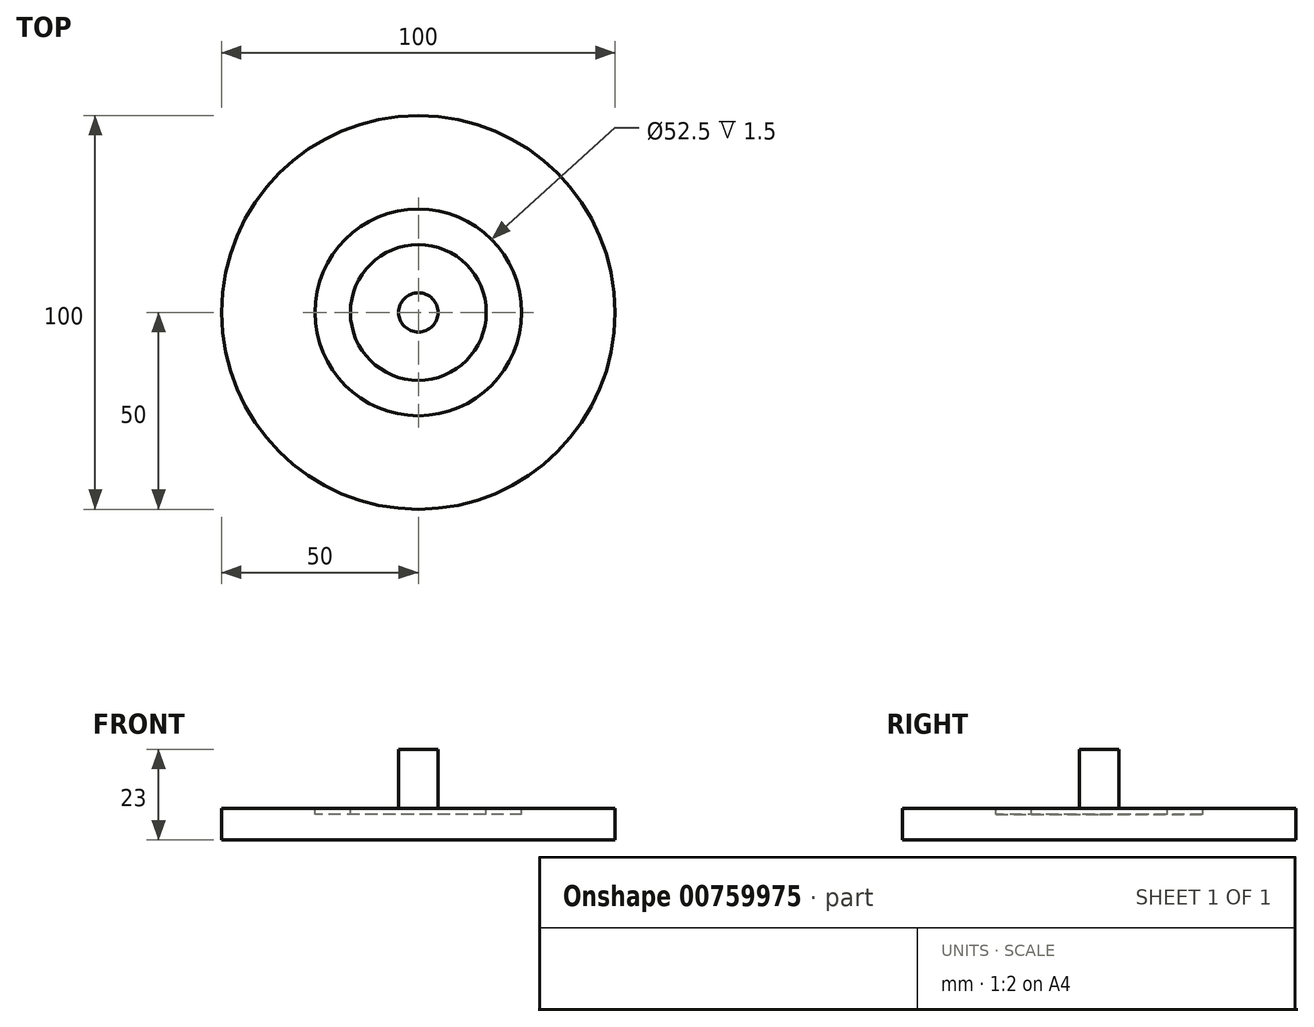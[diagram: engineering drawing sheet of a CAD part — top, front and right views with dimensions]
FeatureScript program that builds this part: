
annotation { "Feature Type Name" : "Feature", "Feature Type Description" : "" }
export const myFeature = defineFeature(function(context is Context, id is Id, definition is map)
    precondition{}
    {
        {
            var Q0;
            Q0=qCreatedBy(makeId("Top.planeOp"),FACE);
            var sketch = newSketch(context, id + "F0", { "sketchPlane" : qUnion([Q0])});
            skCircle(sketch, "E0", {"center": v(0, 0) * mm, "radius": 50 * mm});
            skSolve(sketch);
        }
        {
            var Q0;
            Q0=makeQuery(id+"F0.imprint","IMPRINT",FACE,{"disambiguationData":[TD([[makeQuery(id+"F0.imprint","IMPRINT",EDGE,{"derivedFrom":sQuery(id+"F0.wireOp",EDGE,"E0")}),1.0]])]});
            extrude(context, id + "F1", {"entities" : qUnion([Q0]), "depth" : 8 * mm, "offsetDistance" : 25.4 * mm});
        }
        {
            var Q0;
            Q0=makeQuery(id+"F1.opExtrude","CAP_FACE",FACE,{"disambiguationData":[OSD([sQuery(id+"F0.wireOp",EDGE,"E0")])],"isStart":false});
            var sketch = newSketch(context, id + "F2", { "sketchPlane" : qUnion([Q0])});
            skCircle(sketch, "E1", {"center": v(0, 0) * mm, "radius": 26.25 * mm});
            skCircle(sketch, "E2", {"center": v(0, 0) * mm, "radius": 17.25 * mm});
            skSolve(sketch);
        }
        {
            var Q0;
            Q0=makeQuery(id+"F2.imprint","IMPRINT",FACE,{"disambiguationData":[TD([[makeQuery(id+"F2.imprint","IMPRINT",EDGE,{"derivedFrom":sQuery(id+"F2.wireOp",EDGE,"E1")}),1.0]])]});
            extrude(context, id + "F3", {"entities" : qUnion([Q0]), "operationType" : NewBodyOperationType.REMOVE, "oppositeDirection" : true, "depth" : 1.5 * mm, "offsetDistance" : 25 * mm});
        }
        {
            var Q0;
            Q0=makeQuery(id+"F3.boolean.opBoolean","SPLIT",FACE,{"disambiguationData":[TD([makeQuery(id+"F3.opExtrude","SWEPT_FACE",FACE,{"disambiguationData":[OSD([sQuery(id+"F2.wireOp",EDGE,"E2")])]})])],"derivedFrom":makeQuery(id+"F1.opExtrude","CAP_FACE",FACE,{"disambiguationData":[OSD([sQuery(id+"F0.wireOp",EDGE,"E0")])],"isStart":false})});
            var sketch = newSketch(context, id + "F4", { "sketchPlane" : qUnion([Q0])});
            skCircle(sketch, "E3", {"center": v(0, 0) * mm, "radius": 5 * mm});
            skSolve(sketch);
        }
        {
            var Q0;
            Q0=makeQuery(id+"F4.imprint","IMPRINT",FACE,{"disambiguationData":[TD([[makeQuery(id+"F4.imprint","IMPRINT",EDGE,{"derivedFrom":sQuery(id+"F4.wireOp",EDGE,"E3")}),1.0]])]});
            extrude(context, id + "F5", {"entities" : qUnion([Q0]), "operationType" : NewBodyOperationType.ADD, "depth" : 15 * mm, "offsetDistance" : 25 * mm});
        }
    });
